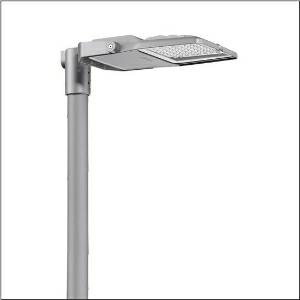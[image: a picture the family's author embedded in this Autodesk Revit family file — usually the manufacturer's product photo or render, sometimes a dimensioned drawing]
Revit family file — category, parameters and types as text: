
# Revit family: floodlight_fl_21_mini___pl61_5xa7772d2c3a_4a46
name_source: partatom
category: Lighting Fixtures
units: mm (PartAtom-declared; Revit-internal decimal feet)

## family parameters
Cut with Voids When Loaded = No
Host = Face
Light Source = No
Part Type = Normal
Room Calculation Point = No
Round Connector Dimension = Use Diameter
Shared = No

## types (1)
- --- (1 x LED, 17500 lm, 143 W, 3000K)
    Apparent Load = 143 VA
    CIE Flux Codes = 33 65 98 100 100
    Color Rendering = 70
    Color Temperature = 3000K
    Default Elevation = 1800 mm
    Description = Floodlight FL 21 mini, floodlight, primary light control with lens, of PMMA, primary optical cover: protective disc, of toughened safety glass, transparent, light distribution: PL61, light emission: direct distribution, installation type: surface-mounted, LED, High Power LED, rated luminous flux: 17.500lm, luminous efficacy: 122lm/W, light colour: 730, colour temperature: 3000K, control gear: ECG iQ, control: Auto-Match, Temp-Guard, Night-Set, Smart-Wire, Desk-Remote (wireless, voltage-free reading and setting of iQ features in the workshop via application-optimized NFC function/RFID function), optimised constant luminous flux control (CLO 2.0), Light-Fading, Lumen-Switch, with terminal, 6-pole, mains connection: 220..240V, AC, 50/60Hz, start of lifetime: 143W, end of lifetime: 152W, reduction: 61W, luminaire housing, of diecast aluminium, powder-coated, Siteco® metallic grey (DB 702S), corrosivity category C5 according to DIN EN ISO 12944, mast bracket, of steel, galvanised, powder-coated, protection rating (complete): IP66, insulation class (complete): insulation class II (safety insulation), certification: CE, ENEC, VDE, protection symbol: D, impact resistance: IK08, permissible operating ambient temperature: -40..+40°C, permissible operating ambient temperature for outdoor applications: -40..+50°C, standard: DIN EN 12944, packaging unit: 1 piece

Light Distribution: PL61
    Height = 70 mm
    Lamp = 1 x LED
    Lamp Light Flux = 17500 lm
    Lamp Power = 143 W
    Lamp count = 1
    Length = 485 mm
    Luminous efficacy = 122 lm/W
    Manufacturer = Siteco
    ModVariant = No
    Model = 5XA7772D2C3A
    Number of Poles = 1
    OnlyDefault = Yes
    Power Factor = 1
    Product Name = Floodlight FL 21 mini | PL61
    Product group = floodlight | pylon top
    ProductGroupID = 6101
    Protection Class = Protection class II
    Protection Degree = IP 66
    RLX_Detail_Level = 1
    RlxData = <blob elided: 101425 chars, md5=baaccff0>
    Socket = socket
    Standby Power = 0 W
    System Light Flux = 17500 lm
    System Power = 143 W
    Type Comments = factory setting: luminous flux: 100 % | dim-lin: 254 | 730 mA
    Type Image = l_1007125.jpg
    URL = http://relux.com
    VarID = @adj_084777
    Voltage = 0 V
    Weight = 0.00 kg
    Width = 337 mm

## geometry (parser evidence)
native form markers: Blend x4, Sweep x12
no freeform markers — native parametric forms only
